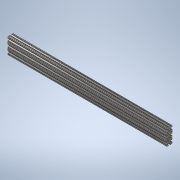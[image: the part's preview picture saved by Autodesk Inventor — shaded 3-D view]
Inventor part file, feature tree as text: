
AUTODESK INVENTOR PART (.ipt)
format: ipt  version: 2020 (Build 240168000, 168)  size: 390,656 bytes
history: native  units: in
note: dims shown in document units (in); Inventor stores cm internally (conversion verified against a paired STEP export)
features: sketch x2, extrude x1
ambient origin geometry x8: Origin, YZ Plane, XZ Plane, XY Plane, X Axis, Y Axis, Z Axis, Center Point
bodies: Solid1 (feature_tree)
feature tree (3):
  extrude  "Extrusion1"  [1 undecoded]
  sketch  "Sketch2"
  sketch  "Sketch1"  dims[d0=29.0in d1=0.0in]
note: 1 required parameter value undecoded (feature->parameter linkage not recoverable at this tier; creation-order binding heuristic only, values carry confidence <= 0.55)
